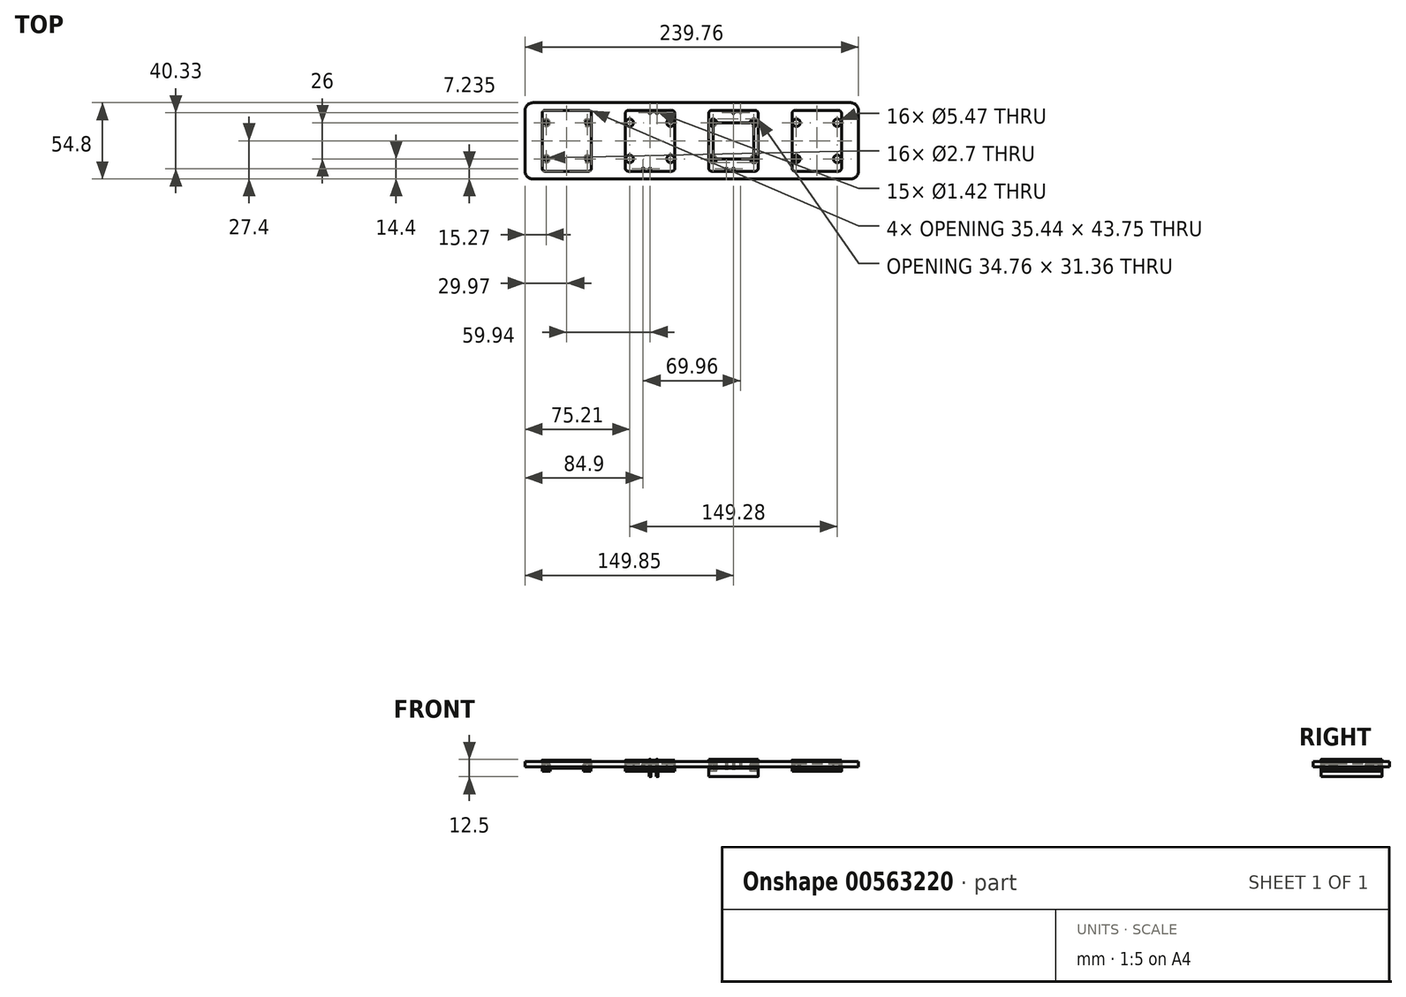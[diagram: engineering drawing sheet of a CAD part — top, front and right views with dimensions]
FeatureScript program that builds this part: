
annotation { "Feature Type Name" : "Feature", "Feature Type Description" : "" }
export const myFeature = defineFeature(function(context is Context, id is Id, definition is map)
    precondition{}
    {
        {
            var Q0;
            Q0=qCreatedBy(makeId("Top.planeOp"),FACE);
            var sketch = newSketch(context, id + "F0", { "sketchPlane" : qUnion([Q0])});
            skLineSegment(sketch, "E0.bottom", {"start": v(105.63, 21.88) * mm, "end": v(74.2, 21.88) * mm});
            skLineSegment(sketch, "E0.top", {"start": v(105.63, -21.88) * mm, "end": v(74.2, -21.88) * mm});
            skLineSegment(sketch, "E0.right", {"start": v(-107.63, 19.88) * mm, "end": v(-107.63, -19.88) * mm});
            skPoint(sketch, "E0.middle", {"position": v(0, 0) * mm});
            skLineSegment(sketch, "E1.left", {"start": v(107.63, 19.88) * mm, "end": v(107.63, -19.88) * mm});
            skPoint(sketch, "E1.middle", {"position": v(89.91, 0) * mm});
            skLineSegment(sketch, "E2.bottom", {"start": v(72.19, 21.88) * mm, "end": v(47.7, 21.88) * mm});
            skLineSegment(sketch, "E2.top", {"start": v(72.19, -21.88) * mm, "end": v(47.7, -21.88) * mm});
            skLineSegment(sketch, "E2.left", {"start": v(72.19, 19.88) * mm, "end": v(72.19, -19.88) * mm});
            skLineSegment(sketch, "E2.right", {"start": v(47.7, 19.88) * mm, "end": v(47.7, -19.88) * mm});
            skPoint(sketch, "E2.middle", {"position": v(59.94, 0) * mm});
            skLineSegment(sketch, "E3.bottom", {"start": v(45.7, 21.88) * mm, "end": v(14.25, 21.88) * mm});
            skLineSegment(sketch, "E3.top", {"start": v(45.7, -21.88) * mm, "end": v(14.25, -21.88) * mm});
            skLineSegment(sketch, "E3.right", {"start": v(12.25, 19.88) * mm, "end": v(12.25, -19.88) * mm});
            skPoint(sketch, "E3.middle", {"position": v(29.97, 0) * mm});
            skLineSegment(sketch, "E4.MirrorCS", {"start": v(-12.25, 19.88) * mm, "end": v(-12.25, -19.88) * mm});
            skLineSegment(sketch, "E5.MirrorCS", {"start": v(-47.7, 19.88) * mm, "end": v(-47.7, -19.88) * mm});
            skLineSegment(sketch, "E6.MirrorCS", {"start": v(-72.19, 19.88) * mm, "end": v(-72.19, -19.88) * mm});
            skLineSegment(sketch, "E7.bottom", {"start": v(114.35, 27.4) * mm, "end": v(-114.35, 27.4) * mm});
            skLineSegment(sketch, "E7.top", {"start": v(114.35, -27.4) * mm, "end": v(-114.35, -27.4) * mm});
            skLineSegment(sketch, "E7.left", {"start": v(119.88, 21.87) * mm, "end": v(119.88, -21.87) * mm});
            skLineSegment(sketch, "E7.right", {"start": v(-119.88, 21.87) * mm, "end": v(-119.88, -21.87) * mm});
            skLineSegment(sketch, "E8.bottom", {"start": v(44.67, 13) * mm, "end": v(15.27, 13) * mm});
            skLineSegment(sketch, "E8.top", {"start": v(44.67, -13) * mm, "end": v(15.27, -13) * mm});
            skLineSegment(sketch, "E8.left", {"start": v(44.67, 13) * mm, "end": v(44.67, -13) * mm});
            skLineSegment(sketch, "E8.right", {"start": v(15.27, 13) * mm, "end": v(15.27, -13) * mm});
            skCircle(sketch, "E9", {"center": v(15.27, 13) * mm, "radius": 2.73 * mm});
            skCircle(sketch, "E10", {"center": v(44.67, 13) * mm, "radius": 2.73 * mm});
            skCircle(sketch, "E11", {"center": v(15.27, -13) * mm, "radius": 2.73 * mm});
            skCircle(sketch, "E12", {"center": v(44.67, -13) * mm, "radius": 2.73 * mm});
            skCircle(sketch, "E13", {"center": v(15.27, 13) * mm, "radius": 1.35 * mm});
            skCircle(sketch, "E14", {"center": v(44.67, 13) * mm, "radius": 1.35 * mm});
            skCircle(sketch, "E15", {"center": v(15.27, -13) * mm, "radius": 1.35 * mm});
            skCircle(sketch, "E16", {"center": v(44.67, -13) * mm, "radius": 1.35 * mm});
            skLineSegment(sketch, "E17.MirrorCS", {"start": v(72.19, -19.88) * mm, "end": v(72.19, 19.88) * mm});
            skLineSegment(sketch, "E18", {"start": v(59.94, -21.88) * mm, "end": v(59.94, 21.88) * mm});
            skCircle(sketch, "E19.MirrorC", {"center": v(75.2, 13) * mm, "radius": 2.73 * mm});
            skCircle(sketch, "E20.MirrorC", {"center": v(75.2, 13) * mm, "radius": 1.35 * mm});
            skCircle(sketch, "E21.MirrorC", {"center": v(104.61, 13) * mm, "radius": 2.73 * mm});
            skCircle(sketch, "E22.MirrorC", {"center": v(104.61, 13) * mm, "radius": 1.35 * mm});
            skCircle(sketch, "E23.MirrorC", {"center": v(104.61, -13) * mm, "radius": 2.73 * mm});
            skCircle(sketch, "E24.MirrorC", {"center": v(104.61, -13) * mm, "radius": 1.35 * mm});
            skCircle(sketch, "E25.MirrorC", {"center": v(75.2, -13) * mm, "radius": 1.35 * mm});
            skCircle(sketch, "E26.MirrorC", {"center": v(75.2, -13) * mm, "radius": 2.73 * mm});
            skCircle(sketch, "E27.MirrorC", {"center": v(-15.27, 13) * mm, "radius": 2.73 * mm});
            skCircle(sketch, "E28.MirrorC", {"center": v(-15.27, 13) * mm, "radius": 1.35 * mm});
            skCircle(sketch, "E29.MirrorC", {"center": v(-15.27, -13) * mm, "radius": 2.73 * mm});
            skCircle(sketch, "E30.MirrorC", {"center": v(-15.27, -13) * mm, "radius": 1.35 * mm});
            skCircle(sketch, "E31.MirrorC", {"center": v(-44.67, -13) * mm, "radius": 2.73 * mm});
            skCircle(sketch, "E32.MirrorC", {"center": v(-44.67, -13) * mm, "radius": 1.35 * mm});
            skCircle(sketch, "E33.MirrorC", {"center": v(-44.67, 13) * mm, "radius": 2.73 * mm});
            skCircle(sketch, "E34.MirrorC", {"center": v(-44.67, 13) * mm, "radius": 1.35 * mm});
            skCircle(sketch, "E35.MirrorC", {"center": v(-75.2, 13) * mm, "radius": 2.73 * mm});
            skCircle(sketch, "E36.MirrorC", {"center": v(-75.2, 13) * mm, "radius": 1.35 * mm});
            skCircle(sketch, "E37.MirrorC", {"center": v(-104.61, 13) * mm, "radius": 1.35 * mm});
            skCircle(sketch, "E38.MirrorC", {"center": v(-104.61, 13) * mm, "radius": 2.73 * mm});
            skCircle(sketch, "E39.MirrorC", {"center": v(-75.2, -13) * mm, "radius": 2.73 * mm});
            skCircle(sketch, "E40.MirrorC", {"center": v(-75.2, -13) * mm, "radius": 1.35 * mm});
            skCircle(sketch, "E41.MirrorC", {"center": v(-104.61, -13) * mm, "radius": 1.35 * mm});
            skCircle(sketch, "E42.MirrorC", {"center": v(-104.61, -13) * mm, "radius": 2.73 * mm});
            skPoint(sketch, "E43.MirrorP", {"position": v(-89.91, 0) * mm});
            skPoint(sketch, "E44.MirrorP", {"position": v(-29.97, 0) * mm});
            skLineSegment(sketch, "E45", {"start": v(29.97, -21.88) * mm, "end": v(29.97, 21.88) * mm});
            skLineSegment(sketch, "E46", {"start": v(29.97, 21.88) * mm, "end": v(29.97, 20.17) * mm});
            skLineSegment(sketch, "E47", {"start": v(29.97, 20.17) * mm, "end": v(34.98, 20.17) * mm});
            skCircle(sketch, "E48", {"center": v(29.97, 20.17) * mm, "radius": 0.71 * mm});
            skCircle(sketch, "E49", {"center": v(34.98, 20.17) * mm, "radius": 0.71 * mm});
            skCircle(sketch, "E50.MirrorC", {"center": v(29.97, -20.17) * mm, "radius": 0.71 * mm});
            skCircle(sketch, "E51.MirrorC", {"center": v(24.96, -20.17) * mm, "radius": 0.71 * mm});
            skCircle(sketch, "E52.MirrorC", {"center": v(-29.97, 20.17) * mm, "radius": 0.71 * mm});
            skCircle(sketch, "E53.MirrorC", {"center": v(-29.97, -20.17) * mm, "radius": 0.71 * mm});
            skCircle(sketch, "E54.MirrorC", {"center": v(-24.96, 20.17) * mm, "radius": 0.71 * mm});
            skCircle(sketch, "E55.MirrorC", {"center": v(-34.98, -20.17) * mm, "radius": 0.71 * mm});
            skLineSegment(sketch, "E56", {"start": v(107.63, 21.88) * mm, "end": v(119.88, 21.88) * mm});
            skPoint(sketch, "E57.visualSharp", {"position": v(119.88, 27.4) * mm});
            skArc(sketch, "E57.filletArc", {"start": v(119.88, 21.87) * mm, "mid": v(118.26, 25.78) * mm, "end": v(114.35, 27.4) * mm});
            skPoint(sketch, "E58.visualSharp", {"position": v(119.88, -27.4) * mm});
            skArc(sketch, "E58.filletArc", {"start": v(114.35, -27.4) * mm, "mid": v(118.26, -25.78) * mm, "end": v(119.88, -21.87) * mm});
            skArc(sketch, "E59.MirrorCS", {"start": v(-119.88, 21.87) * mm, "mid": v(-118.26, 25.78) * mm, "end": v(-114.35, 27.4) * mm});
            skArc(sketch, "E60.MirrorCS", {"start": v(-114.35, -27.4) * mm, "mid": v(-118.26, -25.78) * mm, "end": v(-119.88, -21.87) * mm});
            skPoint(sketch, "E61.orphan", {"position": v(-119.88, 27.4) * mm});
            skPoint(sketch, "E62.orphan", {"position": v(-119.88, -27.4) * mm});
            skPoint(sketch, "E63.visualSharp", {"position": v(12.25, 21.88) * mm});
            skArc(sketch, "E63.filletArc", {"start": v(14.25, 21.88) * mm, "mid": v(12.84, 21.29) * mm, "end": v(12.25, 19.88) * mm});
            skPoint(sketch, "E64.orphan", {"position": v(0, 21.88) * mm});
            skPoint(sketch, "E65.end.orphan", {"position": v(0, -21.88) * mm});
            skArc(sketch, "E66.MirrorCS", {"start": v(45.7, 21.88) * mm, "mid": v(47.1, 21.29) * mm, "end": v(47.7, 19.88) * mm});
            skArc(sketch, "E67.MirrorCS", {"start": v(14.25, -21.88) * mm, "mid": v(12.84, -21.29) * mm, "end": v(12.25, -19.88) * mm});
            skArc(sketch, "E68.MirrorCS", {"start": v(45.7, -21.88) * mm, "mid": v(47.1, -21.29) * mm, "end": v(47.7, -19.88) * mm});
            skArc(sketch, "E69.MirrorCS", {"start": v(74.2, 21.88) * mm, "mid": v(72.78, 21.29) * mm, "end": v(72.19, 19.88) * mm});
            skArc(sketch, "E70.MirrorCS", {"start": v(105.63, 21.88) * mm, "mid": v(107.04, 21.29) * mm, "end": v(107.63, 19.88) * mm});
            skArc(sketch, "E71.MirrorCS", {"start": v(74.2, -21.88) * mm, "mid": v(72.78, -21.29) * mm, "end": v(72.19, -19.88) * mm});
            skArc(sketch, "E72.MirrorCS", {"start": v(105.63, -21.88) * mm, "mid": v(107.04, -21.29) * mm, "end": v(107.63, -19.88) * mm});
            skArc(sketch, "E73.MirrorCS", {"start": v(-14.25, 21.88) * mm, "mid": v(-12.84, 21.29) * mm, "end": v(-12.25, 19.88) * mm});
            skArc(sketch, "E74.MirrorCS", {"start": v(-45.7, 21.88) * mm, "mid": v(-47.1, 21.29) * mm, "end": v(-47.7, 19.88) * mm});
            skArc(sketch, "E75.MirrorCS", {"start": v(-74.2, 21.88) * mm, "mid": v(-72.78, 21.29) * mm, "end": v(-72.19, 19.88) * mm});
            skArc(sketch, "E76.MirrorCS", {"start": v(-105.63, 21.88) * mm, "mid": v(-107.04, 21.29) * mm, "end": v(-107.63, 19.88) * mm});
            skArc(sketch, "E77.MirrorCS", {"start": v(-14.25, -21.88) * mm, "mid": v(-12.84, -21.29) * mm, "end": v(-12.25, -19.88) * mm});
            skArc(sketch, "E78.MirrorCS", {"start": v(-45.7, -21.88) * mm, "mid": v(-47.1, -21.29) * mm, "end": v(-47.7, -19.88) * mm});
            skArc(sketch, "E79.MirrorCS", {"start": v(-74.2, -21.88) * mm, "mid": v(-72.78, -21.29) * mm, "end": v(-72.19, -19.88) * mm});
            skArc(sketch, "E80.MirrorCS", {"start": v(-105.63, -21.88) * mm, "mid": v(-107.04, -21.29) * mm, "end": v(-107.63, -19.88) * mm});
            skPoint(sketch, "E81.orphan", {"position": v(-107.63, 21.88) * mm});
            skLineSegment(sketch, "E82.trimOffspring", {"start": v(-74.2, 21.88) * mm, "end": v(-105.63, 21.88) * mm});
            skPoint(sketch, "E83.orphan", {"position": v(-47.7, 21.88) * mm});
            skLineSegment(sketch, "E84.trimOffspring", {"start": v(-47.7, 21.88) * mm, "end": v(-72.19, 21.88) * mm});
            skLineSegment(sketch, "E85.trimOffspring", {"start": v(-14.25, 21.88) * mm, "end": v(-45.7, 21.88) * mm});
            skLineSegment(sketch, "E86.trimOffspring", {"start": v(12.25, 21.88) * mm, "end": v(-12.25, 21.88) * mm});
            skPoint(sketch, "E87.orphan", {"position": v(107.63, -21.88) * mm});
            skPoint(sketch, "E88.orphan", {"position": v(72.19, -21.88) * mm});
            skPoint(sketch, "E89.orphan", {"position": v(47.7, -21.88) * mm});
            skLineSegment(sketch, "E90.trimOffspring", {"start": v(12.25, -21.88) * mm, "end": v(-12.25, -21.88) * mm});
            skPoint(sketch, "E91.orphan", {"position": v(-12.25, -21.88) * mm});
            skLineSegment(sketch, "E92.trimOffspring", {"start": v(-14.25, -21.88) * mm, "end": v(-45.7, -21.88) * mm});
            skPoint(sketch, "E93.orphan", {"position": v(-47.7, -21.88) * mm});
            skLineSegment(sketch, "E94.trimOffspring", {"start": v(-47.7, -21.88) * mm, "end": v(-72.19, -21.88) * mm});
            skPoint(sketch, "E95.orphan", {"position": v(-72.19, -21.88) * mm});
            skLineSegment(sketch, "E96.trimOffspring", {"start": v(-74.2, -21.88) * mm, "end": v(-105.63, -21.88) * mm});
            skPoint(sketch, "E97.orphan", {"position": v(-107.63, -21.88) * mm});
            skSolve(sketch);
        }
        {
            var Q0;
            {var subQ0=sQuery(id+"F0.wireOp",EDGE,"E4.MirrorCS");Q0=makeQuery(id+"F0.imprint","IMPRINT",FACE,{"disambiguationData":[TD([[makeQuery(id+"F0.imprint","IMPRINT",EDGE,{"derivedFrom":subQ0}),-1.0]])]});}
            var Q1;
            {var subQ1=sQuery(id+"F0.wireOp",EDGE,"E0.right");Q1=makeQuery(id+"F0.imprint","IMPRINT",FACE,{"disambiguationData":[TD([[makeQuery(id+"F0.imprint","IMPRINT",EDGE,{"derivedFrom":subQ1}),1.0]])]});}
            var Q2;
            {var subQ19=sQuery(id+"F0.wireOp",EDGE,"E3.right");Q2=makeQuery(id+"F0.imprint","IMPRINT",FACE,{"disambiguationData":[TD([[makeQuery(id+"F0.imprint","IMPRINT",EDGE,{"derivedFrom":subQ19}),1.0]])]});}
            var Q3;
            {var subQ14=sQuery(id+"F0.wireOp",EDGE,"E2.right");Q3=makeQuery(id+"F0.imprint","IMPRINT",FACE,{"disambiguationData":[TD([[makeQuery(id+"F0.imprint","IMPRINT",EDGE,{"derivedFrom":subQ14}),-1.0]])]});}
            var Q4;
            {var subQ0=sQuery(id+"F0.wireOp",EDGE,"E10");var subQ1=sQuery(id+"F0.wireOp",EDGE,"E8.bottom");var subQ2=makeQuery(id+"F0.imprint","INTERSECT",VERTEX,{"derivedFrom":[subQ1,subQ0]});Q4=makeQuery(id+"F0.imprint","IMPRINT",FACE,{"disambiguationData":[TD([[makeQuery(id+"F0.imprint","IMPRINT",EDGE,{"disambiguationData":[TD([[subQ2,-1.0]])],"derivedFrom":subQ1}),1.0]])]});}
            var Q5;
            {var subQ5=sQuery(id+"F0.wireOp",EDGE,"E45");var subQ9=sQuery(id+"F0.wireOp",EDGE,"E8.bottom");var subQ11=makeQuery(id+"F0.imprint","INTERSECT",VERTEX,{"derivedFrom":[subQ9,subQ5]});Q5=makeQuery(id+"F0.imprint","IMPRINT",FACE,{"disambiguationData":[TD([[makeQuery(id+"F0.imprint","IMPRINT",EDGE,{"disambiguationData":[TD([[subQ11,-1.0]])],"derivedFrom":subQ9}),1.0]])]});}
            var Q6;
            Q6=makeQuery(id+"F0.imprint","IMPRINT",FACE,{"disambiguationData":[TD([[makeQuery(id+"F0.imprint","IMPRINT",EDGE,{"derivedFrom":sQuery(id+"F0.wireOp",EDGE,"E0.bottom")}),1.0]])]});
            var Q7;
            Q7=makeQuery(id+"F0.imprint","IMPRINT",FACE,{"disambiguationData":[TD([[makeQuery(id+"F0.imprint","IMPRINT",EDGE,{"derivedFrom":sQuery(id+"F0.wireOp",EDGE,"E37.MirrorC")}),-1.0]])]});
            var Q8;
            Q8=makeQuery(id+"F0.imprint","IMPRINT",FACE,{"disambiguationData":[TD([[makeQuery(id+"F0.imprint","IMPRINT",EDGE,{"derivedFrom":sQuery(id+"F0.wireOp",EDGE,"E35.MirrorC")}),1.0]])]});
            var Q9;
            Q9=makeQuery(id+"F0.imprint","IMPRINT",FACE,{"disambiguationData":[TD([[makeQuery(id+"F0.imprint","IMPRINT",EDGE,{"derivedFrom":sQuery(id+"F0.wireOp",EDGE,"E33.MirrorC")}),-1.0]])]});
            var Q10;
            Q10=makeQuery(id+"F0.imprint","IMPRINT",FACE,{"disambiguationData":[TD([[makeQuery(id+"F0.imprint","IMPRINT",EDGE,{"derivedFrom":sQuery(id+"F0.wireOp",EDGE,"E27.MirrorC")}),-1.0]])]});
            var Q11;
            Q11=makeQuery(id+"F0.imprint","IMPRINT",FACE,{"disambiguationData":[TD([[makeQuery(id+"F0.imprint","IMPRINT",EDGE,{"derivedFrom":sQuery(id+"F0.wireOp",EDGE,"E41.MirrorC")}),-1.0]])]});
            var Q12;
            Q12=makeQuery(id+"F0.imprint","IMPRINT",FACE,{"disambiguationData":[TD([[makeQuery(id+"F0.imprint","IMPRINT",EDGE,{"derivedFrom":sQuery(id+"F0.wireOp",EDGE,"E39.MirrorC")}),1.0]])]});
            var Q13;
            Q13=makeQuery(id+"F0.imprint","IMPRINT",FACE,{"disambiguationData":[TD([[makeQuery(id+"F0.imprint","IMPRINT",EDGE,{"derivedFrom":sQuery(id+"F0.wireOp",EDGE,"E31.MirrorC")}),-1.0]])]});
            var Q14;
            Q14=makeQuery(id+"F0.imprint","IMPRINT",FACE,{"disambiguationData":[TD([[makeQuery(id+"F0.imprint","IMPRINT",EDGE,{"derivedFrom":sQuery(id+"F0.wireOp",EDGE,"E29.MirrorC")}),-1.0]])]});
            var Q15;
            {var subQ0=sQuery(id+"F0.wireOp",EDGE,"E11");var subQ1=sQuery(id+"F0.wireOp",EDGE,"E8.top");var subQ2=makeQuery(id+"F0.imprint","INTERSECT",VERTEX,{"derivedFrom":[subQ1,subQ0]});Q15=makeQuery(id+"F0.imprint","IMPRINT",FACE,{"disambiguationData":[TD([[makeQuery(id+"F0.imprint","IMPRINT",EDGE,{"disambiguationData":[TD([[subQ2,-1.0]])],"derivedFrom":subQ1}),-1.0]])]});}
            var Q16;
            {var subQ0=sQuery(id+"F0.wireOp",EDGE,"E11");var subQ1=sQuery(id+"F0.wireOp",EDGE,"E8.top");var subQ2=makeQuery(id+"F0.imprint","INTERSECT",VERTEX,{"derivedFrom":[subQ1,subQ0]});Q16=makeQuery(id+"F0.imprint","IMPRINT",FACE,{"disambiguationData":[TD([[makeQuery(id+"F0.imprint","IMPRINT",EDGE,{"disambiguationData":[TD([[subQ2,-1.0]])],"derivedFrom":subQ1}),1.0]])]});}
            var Q17;
            {var subQ0=sQuery(id+"F0.wireOp",EDGE,"E16");var subQ1=sQuery(id+"F0.wireOp",EDGE,"E8.top");var subQ2=makeQuery(id+"F0.imprint","INTERSECT",VERTEX,{"derivedFrom":[subQ1,subQ0]});Q17=makeQuery(id+"F0.imprint","IMPRINT",FACE,{"disambiguationData":[TD([[makeQuery(id+"F0.imprint","IMPRINT",EDGE,{"disambiguationData":[TD([[subQ2,-1.0]])],"derivedFrom":subQ1}),1.0]])]});}
            var Q18;
            {var subQ0=sQuery(id+"F0.wireOp",EDGE,"E16");var subQ1=sQuery(id+"F0.wireOp",EDGE,"E8.top");var subQ2=makeQuery(id+"F0.imprint","INTERSECT",VERTEX,{"derivedFrom":[subQ1,subQ0]});Q18=makeQuery(id+"F0.imprint","IMPRINT",FACE,{"disambiguationData":[TD([[makeQuery(id+"F0.imprint","IMPRINT",EDGE,{"disambiguationData":[TD([[subQ2,-1.0]])],"derivedFrom":subQ1}),-1.0]])]});}
            var Q19;
            {var subQ0=sQuery(id+"F0.wireOp",EDGE,"E14");var subQ1=sQuery(id+"F0.wireOp",EDGE,"E8.bottom");var subQ2=makeQuery(id+"F0.imprint","INTERSECT",VERTEX,{"derivedFrom":[subQ1,subQ0]});Q19=makeQuery(id+"F0.imprint","IMPRINT",FACE,{"disambiguationData":[TD([[makeQuery(id+"F0.imprint","IMPRINT",EDGE,{"disambiguationData":[TD([[subQ2,-1.0]])],"derivedFrom":subQ1}),1.0]])]});}
            var Q20;
            {var subQ0=sQuery(id+"F0.wireOp",EDGE,"E14");var subQ1=sQuery(id+"F0.wireOp",EDGE,"E8.bottom");var subQ2=makeQuery(id+"F0.imprint","INTERSECT",VERTEX,{"derivedFrom":[subQ1,subQ0]});Q20=makeQuery(id+"F0.imprint","IMPRINT",FACE,{"disambiguationData":[TD([[makeQuery(id+"F0.imprint","IMPRINT",EDGE,{"disambiguationData":[TD([[subQ2,-1.0]])],"derivedFrom":subQ1}),-1.0]])]});}
            var Q21;
            {var subQ0=sQuery(id+"F0.wireOp",EDGE,"E9");var subQ1=sQuery(id+"F0.wireOp",EDGE,"E8.bottom");var subQ2=makeQuery(id+"F0.imprint","INTERSECT",VERTEX,{"derivedFrom":[subQ1,subQ0]});Q21=makeQuery(id+"F0.imprint","IMPRINT",FACE,{"disambiguationData":[TD([[makeQuery(id+"F0.imprint","IMPRINT",EDGE,{"disambiguationData":[TD([[subQ2,-1.0]])],"derivedFrom":subQ1}),-1.0]])]});}
            var Q22;
            {var subQ0=sQuery(id+"F0.wireOp",EDGE,"E9");var subQ1=sQuery(id+"F0.wireOp",EDGE,"E8.bottom");var subQ2=makeQuery(id+"F0.imprint","INTERSECT",VERTEX,{"derivedFrom":[subQ1,subQ0]});Q22=makeQuery(id+"F0.imprint","IMPRINT",FACE,{"disambiguationData":[TD([[makeQuery(id+"F0.imprint","IMPRINT",EDGE,{"disambiguationData":[TD([[subQ2,-1.0]])],"derivedFrom":subQ1}),1.0]])]});}
            var Q23;
            Q23=makeQuery(id+"F0.imprint","IMPRINT",FACE,{"disambiguationData":[TD([[makeQuery(id+"F0.imprint","IMPRINT",EDGE,{"derivedFrom":sQuery(id+"F0.wireOp",EDGE,"E19.MirrorC")}),-1.0]])]});
            var Q24;
            Q24=makeQuery(id+"F0.imprint","IMPRINT",FACE,{"disambiguationData":[TD([[makeQuery(id+"F0.imprint","IMPRINT",EDGE,{"derivedFrom":sQuery(id+"F0.wireOp",EDGE,"E25.MirrorC")}),1.0]])]});
            var Q25;
            Q25=makeQuery(id+"F0.imprint","IMPRINT",FACE,{"disambiguationData":[TD([[makeQuery(id+"F0.imprint","IMPRINT",EDGE,{"derivedFrom":sQuery(id+"F0.wireOp",EDGE,"E23.MirrorC")}),-1.0]])]});
            var Q26;
            Q26=makeQuery(id+"F0.imprint","IMPRINT",FACE,{"disambiguationData":[TD([[makeQuery(id+"F0.imprint","IMPRINT",EDGE,{"derivedFrom":sQuery(id+"F0.wireOp",EDGE,"E21.MirrorC")}),-1.0]])]});
            extrude(context, id + "F1", {"entities" : qUnion([Q0, Q1, Q2, Q3, Q4, Q5, Q6, Q7, Q8, Q9, Q10, Q11, Q12, Q13, Q14, Q15, Q16, Q17, Q18, Q19, Q20, Q21, Q22, Q23, Q24, Q25, Q26]), "endBound" : BoundingType.SYMMETRIC, "depth" : 5.8 * mm, "offsetDistance" : 25 * mm});
        }
        {
            var Q0;
            {var subQ23=sQuery(id+"F0.wireOp",EDGE,"E0.right");Q0=makeQuery(id+"F0.imprint","IMPRINT",FACE,{"disambiguationData":[TD([[makeQuery(id+"F0.imprint","IMPRINT",EDGE,{"derivedFrom":subQ23}),-1.0]])]});}
            var Q1;
            {var subQ0=sQuery(id+"F0.wireOp",EDGE,"E5.MirrorCS");Q1=makeQuery(id+"F0.imprint","IMPRINT",FACE,{"disambiguationData":[TD([[makeQuery(id+"F0.imprint","IMPRINT",EDGE,{"derivedFrom":subQ0}),-1.0]])]});}
            var Q2;
            {var subQ0=sQuery(id+"F0.wireOp",EDGE,"E3.right");Q2=makeQuery(id+"F0.imprint","IMPRINT",FACE,{"disambiguationData":[TD([[makeQuery(id+"F0.imprint","IMPRINT",EDGE,{"derivedFrom":subQ0}),-1.0]])]});}
            var Q3;
            {var subQ0=sQuery(id+"F0.wireOp",EDGE,"E17.MirrorCS");Q3=makeQuery(id+"F0.imprint","IMPRINT",FACE,{"disambiguationData":[TD([[makeQuery(id+"F0.imprint","IMPRINT",EDGE,{"derivedFrom":subQ0}),1.0]])]});}
            var Q4;
            {var subQ0=sQuery(id+"F0.wireOp",EDGE,"E2.right");Q4=makeQuery(id+"F0.imprint","IMPRINT",FACE,{"disambiguationData":[TD([[makeQuery(id+"F0.imprint","IMPRINT",EDGE,{"derivedFrom":subQ0}),1.0]])]});}
            extrude(context, id + "F2", {"entities" : qUnion([Q0, Q1, Q2, Q3, Q4]), "endBound" : BoundingType.SYMMETRIC, "oppositeDirection" : true, "depth" : 4 * mm, "offsetDistance" : 25 * mm});
        }
        {
            var Q0;
            Q0=makeQuery(id+"F0.imprint","IMPRINT",FACE,{"disambiguationData":[TD([[makeQuery(id+"F0.imprint","IMPRINT",EDGE,{"derivedFrom":sQuery(id+"F0.wireOp",EDGE,"E41.MirrorC")}),-1.0]])]});
            var Q1;
            Q1=makeQuery(id+"F0.imprint","IMPRINT",FACE,{"disambiguationData":[TD([[makeQuery(id+"F0.imprint","IMPRINT",EDGE,{"derivedFrom":sQuery(id+"F0.wireOp",EDGE,"E37.MirrorC")}),-1.0]])]});
            var Q2;
            Q2=makeQuery(id+"F0.imprint","IMPRINT",FACE,{"disambiguationData":[TD([[makeQuery(id+"F0.imprint","IMPRINT",EDGE,{"derivedFrom":sQuery(id+"F0.wireOp",EDGE,"E35.MirrorC")}),1.0]])]});
            var Q3;
            Q3=makeQuery(id+"F0.imprint","IMPRINT",FACE,{"disambiguationData":[TD([[makeQuery(id+"F0.imprint","IMPRINT",EDGE,{"derivedFrom":sQuery(id+"F0.wireOp",EDGE,"E39.MirrorC")}),1.0]])]});
            var Q4;
            Q4=makeQuery(id+"F0.imprint","IMPRINT",FACE,{"disambiguationData":[TD([[makeQuery(id+"F0.imprint","IMPRINT",EDGE,{"derivedFrom":sQuery(id+"F0.wireOp",EDGE,"E31.MirrorC")}),-1.0]])]});
            var Q5;
            Q5=makeQuery(id+"F0.imprint","IMPRINT",FACE,{"disambiguationData":[TD([[makeQuery(id+"F0.imprint","IMPRINT",EDGE,{"derivedFrom":sQuery(id+"F0.wireOp",EDGE,"E29.MirrorC")}),-1.0]])]});
            var Q6;
            Q6=makeQuery(id+"F0.imprint","IMPRINT",FACE,{"disambiguationData":[TD([[makeQuery(id+"F0.imprint","IMPRINT",EDGE,{"derivedFrom":sQuery(id+"F0.wireOp",EDGE,"E33.MirrorC")}),-1.0]])]});
            var Q7;
            Q7=makeQuery(id+"F0.imprint","IMPRINT",FACE,{"disambiguationData":[TD([[makeQuery(id+"F0.imprint","IMPRINT",EDGE,{"derivedFrom":sQuery(id+"F0.wireOp",EDGE,"E27.MirrorC")}),-1.0]])]});
            var Q8;
            {var subQ0=sQuery(id+"F0.wireOp",EDGE,"E9");var subQ1=sQuery(id+"F0.wireOp",EDGE,"E8.bottom");var subQ2=makeQuery(id+"F0.imprint","INTERSECT",VERTEX,{"derivedFrom":[subQ1,subQ0]});Q8=makeQuery(id+"F0.imprint","IMPRINT",FACE,{"disambiguationData":[TD([[makeQuery(id+"F0.imprint","IMPRINT",EDGE,{"disambiguationData":[TD([[subQ2,-1.0]])],"derivedFrom":subQ1}),-1.0]])]});}
            var Q9;
            {var subQ0=sQuery(id+"F0.wireOp",EDGE,"E9");var subQ1=sQuery(id+"F0.wireOp",EDGE,"E8.bottom");var subQ2=makeQuery(id+"F0.imprint","INTERSECT",VERTEX,{"derivedFrom":[subQ1,subQ0]});Q9=makeQuery(id+"F0.imprint","IMPRINT",FACE,{"disambiguationData":[TD([[makeQuery(id+"F0.imprint","IMPRINT",EDGE,{"disambiguationData":[TD([[subQ2,-1.0]])],"derivedFrom":subQ1}),1.0]])]});}
            var Q10;
            {var subQ0=sQuery(id+"F0.wireOp",EDGE,"E11");var subQ1=sQuery(id+"F0.wireOp",EDGE,"E8.top");var subQ2=makeQuery(id+"F0.imprint","INTERSECT",VERTEX,{"derivedFrom":[subQ1,subQ0]});Q10=makeQuery(id+"F0.imprint","IMPRINT",FACE,{"disambiguationData":[TD([[makeQuery(id+"F0.imprint","IMPRINT",EDGE,{"disambiguationData":[TD([[subQ2,-1.0]])],"derivedFrom":subQ1}),1.0]])]});}
            var Q11;
            {var subQ0=sQuery(id+"F0.wireOp",EDGE,"E11");var subQ1=sQuery(id+"F0.wireOp",EDGE,"E8.top");var subQ2=makeQuery(id+"F0.imprint","INTERSECT",VERTEX,{"derivedFrom":[subQ1,subQ0]});Q11=makeQuery(id+"F0.imprint","IMPRINT",FACE,{"disambiguationData":[TD([[makeQuery(id+"F0.imprint","IMPRINT",EDGE,{"disambiguationData":[TD([[subQ2,-1.0]])],"derivedFrom":subQ1}),-1.0]])]});}
            var Q12;
            {var subQ0=sQuery(id+"F0.wireOp",EDGE,"E16");var subQ1=sQuery(id+"F0.wireOp",EDGE,"E8.top");var subQ2=makeQuery(id+"F0.imprint","INTERSECT",VERTEX,{"derivedFrom":[subQ1,subQ0]});Q12=makeQuery(id+"F0.imprint","IMPRINT",FACE,{"disambiguationData":[TD([[makeQuery(id+"F0.imprint","IMPRINT",EDGE,{"disambiguationData":[TD([[subQ2,-1.0]])],"derivedFrom":subQ1}),1.0]])]});}
            var Q13;
            {var subQ0=sQuery(id+"F0.wireOp",EDGE,"E16");var subQ1=sQuery(id+"F0.wireOp",EDGE,"E8.top");var subQ2=makeQuery(id+"F0.imprint","INTERSECT",VERTEX,{"derivedFrom":[subQ1,subQ0]});Q13=makeQuery(id+"F0.imprint","IMPRINT",FACE,{"disambiguationData":[TD([[makeQuery(id+"F0.imprint","IMPRINT",EDGE,{"disambiguationData":[TD([[subQ2,-1.0]])],"derivedFrom":subQ1}),-1.0]])]});}
            var Q14;
            {var subQ0=sQuery(id+"F0.wireOp",EDGE,"E14");var subQ1=sQuery(id+"F0.wireOp",EDGE,"E8.bottom");var subQ2=makeQuery(id+"F0.imprint","INTERSECT",VERTEX,{"derivedFrom":[subQ1,subQ0]});Q14=makeQuery(id+"F0.imprint","IMPRINT",FACE,{"disambiguationData":[TD([[makeQuery(id+"F0.imprint","IMPRINT",EDGE,{"disambiguationData":[TD([[subQ2,-1.0]])],"derivedFrom":subQ1}),-1.0]])]});}
            var Q15;
            {var subQ0=sQuery(id+"F0.wireOp",EDGE,"E14");var subQ1=sQuery(id+"F0.wireOp",EDGE,"E8.bottom");var subQ2=makeQuery(id+"F0.imprint","INTERSECT",VERTEX,{"derivedFrom":[subQ1,subQ0]});Q15=makeQuery(id+"F0.imprint","IMPRINT",FACE,{"disambiguationData":[TD([[makeQuery(id+"F0.imprint","IMPRINT",EDGE,{"disambiguationData":[TD([[subQ2,-1.0]])],"derivedFrom":subQ1}),1.0]])]});}
            var Q16;
            Q16=makeQuery(id+"F0.imprint","IMPRINT",FACE,{"disambiguationData":[TD([[makeQuery(id+"F0.imprint","IMPRINT",EDGE,{"derivedFrom":sQuery(id+"F0.wireOp",EDGE,"E25.MirrorC")}),1.0]])]});
            var Q17;
            Q17=makeQuery(id+"F0.imprint","IMPRINT",FACE,{"disambiguationData":[TD([[makeQuery(id+"F0.imprint","IMPRINT",EDGE,{"derivedFrom":sQuery(id+"F0.wireOp",EDGE,"E23.MirrorC")}),-1.0]])]});
            var Q18;
            Q18=makeQuery(id+"F0.imprint","IMPRINT",FACE,{"disambiguationData":[TD([[makeQuery(id+"F0.imprint","IMPRINT",EDGE,{"derivedFrom":sQuery(id+"F0.wireOp",EDGE,"E19.MirrorC")}),-1.0]])]});
            var Q19;
            Q19=makeQuery(id+"F0.imprint","IMPRINT",FACE,{"disambiguationData":[TD([[makeQuery(id+"F0.imprint","IMPRINT",EDGE,{"derivedFrom":sQuery(id+"F0.wireOp",EDGE,"E21.MirrorC")}),-1.0]])]});
            extrude(context, id + "F3", {"entities" : qUnion([Q0, Q1, Q2, Q3, Q4, Q5, Q6, Q7, Q8, Q9, Q10, Q11, Q12, Q13, Q14, Q15, Q16, Q17, Q18, Q19]), "oppositeDirection" : true, "depth" : 5.1 * mm, "offsetDistance" : 25 * mm});
        }
        {
            var Q0;
            Q0=makeQuery(id+"F0.imprint","IMPRINT",FACE,{"disambiguationData":[TD([[makeQuery(id+"F0.imprint","IMPRINT",EDGE,{"derivedFrom":sQuery(id+"F0.wireOp",EDGE,"E54.MirrorC")}),1.0]])]});
            var Q1;
            Q1=makeQuery(id+"F0.imprint","IMPRINT",FACE,{"disambiguationData":[TD([[makeQuery(id+"F0.imprint","IMPRINT",EDGE,{"derivedFrom":sQuery(id+"F0.wireOp",EDGE,"E49")}),1.0]])]});
            var Q2;
            {var subQ0=sQuery(id+"F0.wireOp",EDGE,"E50.MirrorC");var subQ1=sQuery(id+"F0.wireOp",EDGE,"E45");var subQ2=makeQuery(id+"F0.imprint","INTERSECT",VERTEX,{"disambiguationData":[OD(0.0)],"derivedFrom":[subQ1,subQ0]});Q2=makeQuery(id+"F0.imprint","IMPRINT",FACE,{"disambiguationData":[TD([[makeQuery(id+"F0.imprint","IMPRINT",EDGE,{"disambiguationData":[TD([[subQ2,-1.0]])],"derivedFrom":subQ1}),1.0]])]});}
            var Q3;
            {var subQ0=sQuery(id+"F0.wireOp",EDGE,"E50.MirrorC");var subQ1=sQuery(id+"F0.wireOp",EDGE,"E45");var subQ2=makeQuery(id+"F0.imprint","INTERSECT",VERTEX,{"disambiguationData":[OD(0.0)],"derivedFrom":[subQ1,subQ0]});Q3=makeQuery(id+"F0.imprint","IMPRINT",FACE,{"disambiguationData":[TD([[makeQuery(id+"F0.imprint","IMPRINT",EDGE,{"disambiguationData":[TD([[subQ2,-1.0]])],"derivedFrom":subQ1}),-1.0]])]});}
            var Q4;
            Q4=makeQuery(id+"F0.imprint","IMPRINT",FACE,{"disambiguationData":[TD([[makeQuery(id+"F0.imprint","IMPRINT",EDGE,{"derivedFrom":sQuery(id+"F0.wireOp",EDGE,"E53.MirrorC")}),1.0]])]});
            extrude(context, id + "F4", {"entities" : qUnion([Q0, Q1, Q2, Q3, Q4]), "depth" : 3.5 * mm, "offsetDistance" : 25 * mm, "hasSecondDirection" : true, "secondDirectionOppositeDirection" : true, "secondDirectionDepth" : 9 * mm});
        }
    });
